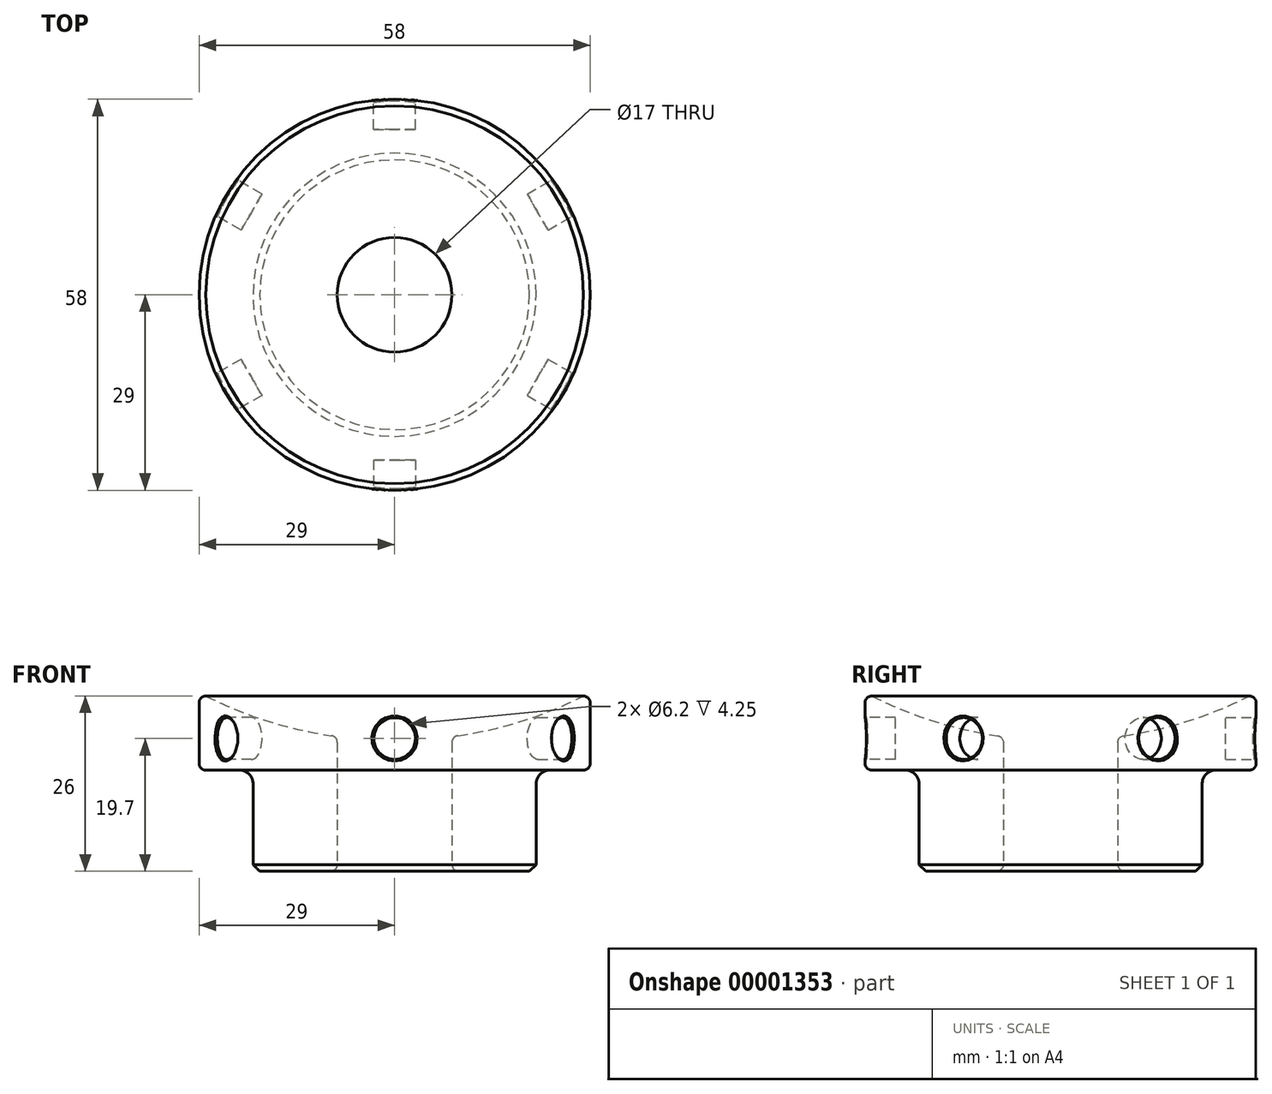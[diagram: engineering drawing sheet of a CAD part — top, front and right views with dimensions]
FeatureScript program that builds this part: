
annotation { "Feature Type Name" : "Feature", "Feature Type Description" : "" }
export const myFeature = defineFeature(function(context is Context, id is Id, definition is map)
    precondition{}
    {
        {
            var Q0;
            Q0=qCreatedBy(makeId("Front.planeOp"),FACE);
            var sketch = newSketch(context, id + "F0", { "sketchPlane" : qUnion([Q0])});
            skLineSegment(sketch, "E0", {"start": v(8.5, 0) * mm, "end": v(21, 0) * mm});
            skLineSegment(sketch, "E1", {"start": v(21, 0) * mm, "end": v(21, 15) * mm});
            skLineSegment(sketch, "E2", {"start": v(21, 15) * mm, "end": v(29, 15) * mm});
            skLineSegment(sketch, "E3", {"start": v(29, 15) * mm, "end": v(29, 26) * mm});
            skLineSegment(sketch, "E4", {"start": v(8.5, 0) * mm, "end": v(8.5, 20) * mm});
            skLineSegment(sketch, "E5", {"start": v(0, 0) * mm, "end": v(0, 27.52) * mm, "construction": true});
            skLineSegment(sketch, "E6", {"start": v(29, 26) * mm, "end": v(28, 26) * mm});
            skArc(sketch, "E7", {"start": v(8.5, 20) * mm, "mid": v(18.5, 22.17) * mm, "end": v(28, 26) * mm});
            skSolve(sketch);
        }
        {
            var Q0;
            Q0 = qSketchRegion(id + "F0", true);
            var Q1;
            Q1=sQuery(id+"F0.wireOp",EDGE,"E5");
            revolve(context, id + "F1", {"entities" : qUnion([Q0]), "axis" : qUnion([Q1]), "revolveType" : RevolveType.FULL});
        }
        {
            var Q0;
            Q0=makeQuery(id+"F1.opRevolve","SWEPT_EDGE",EDGE,{"disambiguationData":[OSD([sQuery(id+"F0.wireOp",EDGE,"E0"),sQuery(id+"F0.wireOp",EDGE,"E4")])]});
            var Q1;
            Q1=makeQuery(id+"F1.opRevolve","SWEPT_EDGE",EDGE,{"disambiguationData":[OSD([sQuery(id+"F0.wireOp",EDGE,"E4"),sQuery(id+"F0.wireOp",EDGE,"E7")])]});
            var Q2;
            Q2=makeQuery(id+"F1.opRevolve","SWEPT_EDGE",EDGE,{"disambiguationData":[OSD([sQuery(id+"F0.wireOp",EDGE,"E2"),sQuery(id+"F0.wireOp",EDGE,"E3")])]});
            var Q3;
            Q3=makeQuery(id+"F1.opRevolve","SWEPT_EDGE",EDGE,{"disambiguationData":[OSD([sQuery(id+"F0.wireOp",EDGE,"E3"),sQuery(id+"F0.wireOp",EDGE,"E6")])]});
            fillet(context, id + "F2", {"entities" : qUnion([Q0, Q1, Q2, Q3]), "radius" : 1 * mm, "tangentPropagation" : true, "allowEdgeOverflow" : false});
        }
        {
            var Q0;
            Q0=makeQuery(id+"F1.opRevolve","SWEPT_EDGE",EDGE,{"disambiguationData":[OSD([sQuery(id+"F0.wireOp",EDGE,"E1"),sQuery(id+"F0.wireOp",EDGE,"E2")])]});
            fillet(context, id + "F3", {"entities" : qUnion([Q0]), "radius" : 2 * mm, "tangentPropagation" : true, "allowEdgeOverflow" : false});
        }
        {
            var Q0;
            Q0=makeQuery(id+"F1.opRevolve","SWEPT_EDGE",EDGE,{"disambiguationData":[OSD([sQuery(id+"F0.wireOp",EDGE,"E0"),sQuery(id+"F0.wireOp",EDGE,"E1")])]});
            chamfer(context, id + "F4", {"entities" : qUnion([Q0]), "width" : 1 * mm, "tangentPropagation" : true});
        }
        {
            var Q0;
            Q0=qCreatedBy(makeId("Front.planeOp"),FACE);
            cPlane(context, id + "F5", {"entities" : qUnion([Q0]), "cplaneType" : CPlaneType.OFFSET, "offset" : 58 / 2 * mm, "width" : 150 * mm, "height" : 150 * mm});
        }
        {
            var Q0;
            Q0=qCreatedBy(id+"F5.planeOp",FACE);
            var sketch = newSketch(context, id + "F6", { "sketchPlane" : qUnion([Q0])});
            skLineSegment(sketch, "E8", {"start": v(0, 0) * mm, "end": v(0, 19.7) * mm, "construction": true});
            skCircle(sketch, "E9", {"center": v(0, 19.7) * mm, "radius": 3.1 * mm});
            skSolve(sketch);
        }
        {
            var Q0;
            Q0=qCreatedBy(makeId("Front.planeOp"),FACE);
            var sketch = newSketch(context, id + "F7", { "sketchPlane" : qUnion([Q0])});
            skLineSegment(sketch, "E10", {"start": v(0, 0) * mm, "end": v(0, 20.8) * mm, "construction": true});
            skSolve(sketch);
        }
        {
            var Q0;
            Q0 = qSketchRegion(id + "F6", true);
            extrude(context, id + "F8", {"entities" : qUnion([Q0]), "operationType" : NewBodyOperationType.REMOVE, "oppositeDirection" : true, "depth" : 4.5 * mm});
        }
        {
            var Q0;
            Q0=makeQuery(id+"F8.boolean.opBoolean","INTERSECT",EDGE,{"derivedFrom":[makeQuery(id+"F1.opRevolve","SWEPT_FACE",FACE,{"disambiguationData":[OSD([sQuery(id+"F0.wireOp",EDGE,"E3")])]}),makeQuery(id+"F8.opExtrude","SWEPT_FACE",FACE,{"disambiguationData":[OSD([sQuery(id+"F6.wireOp",EDGE,"E9")])]})]});
            chamfer(context, id + "F9", {"entities" : qUnion([Q0]), "width" : 0.25 * mm, "tangentPropagation" : true});
        }
        {
            var Q0;
            Q0=makeQuery(id+"F8.boolean.opBoolean","COPY",FACE,{"derivedFrom":makeQuery(id+"F8.opExtrude","SWEPT_FACE",FACE,{"disambiguationData":[OSD([sQuery(id+"F6.wireOp",EDGE,"E9")])]})});
            var Q1;
            Q1=makeQuery(id+"F8.boolean.opBoolean","COPY",FACE,{"derivedFrom":makeQuery(id+"F8.opExtrude","CAP_FACE",FACE,{"disambiguationData":[OSD([sQuery(id+"F6.wireOp",EDGE,"E9")])],"isStart":false})});
            var Q2;
            Q2=makeQuery(id+"F9.opChamfer","BLEND_FACE",FACE,{"disambiguationData":[OSD([sQuery(id+"F0.wireOp",EDGE,"E3"),sQuery(id+"F6.wireOp",EDGE,"E9")])]});
            var Q3;
            Q3=sQuery(id+"F7.wireOp",EDGE,"E10");
            circularPattern(context, id + "F10", {"faces" : qUnion([Q0, Q1, Q2]), "axis" : qUnion([Q3]), "angle" : 360 / 6 * degree, "instanceCount" : 6, "patternType" : PatternType.FACE});
        }
    });
